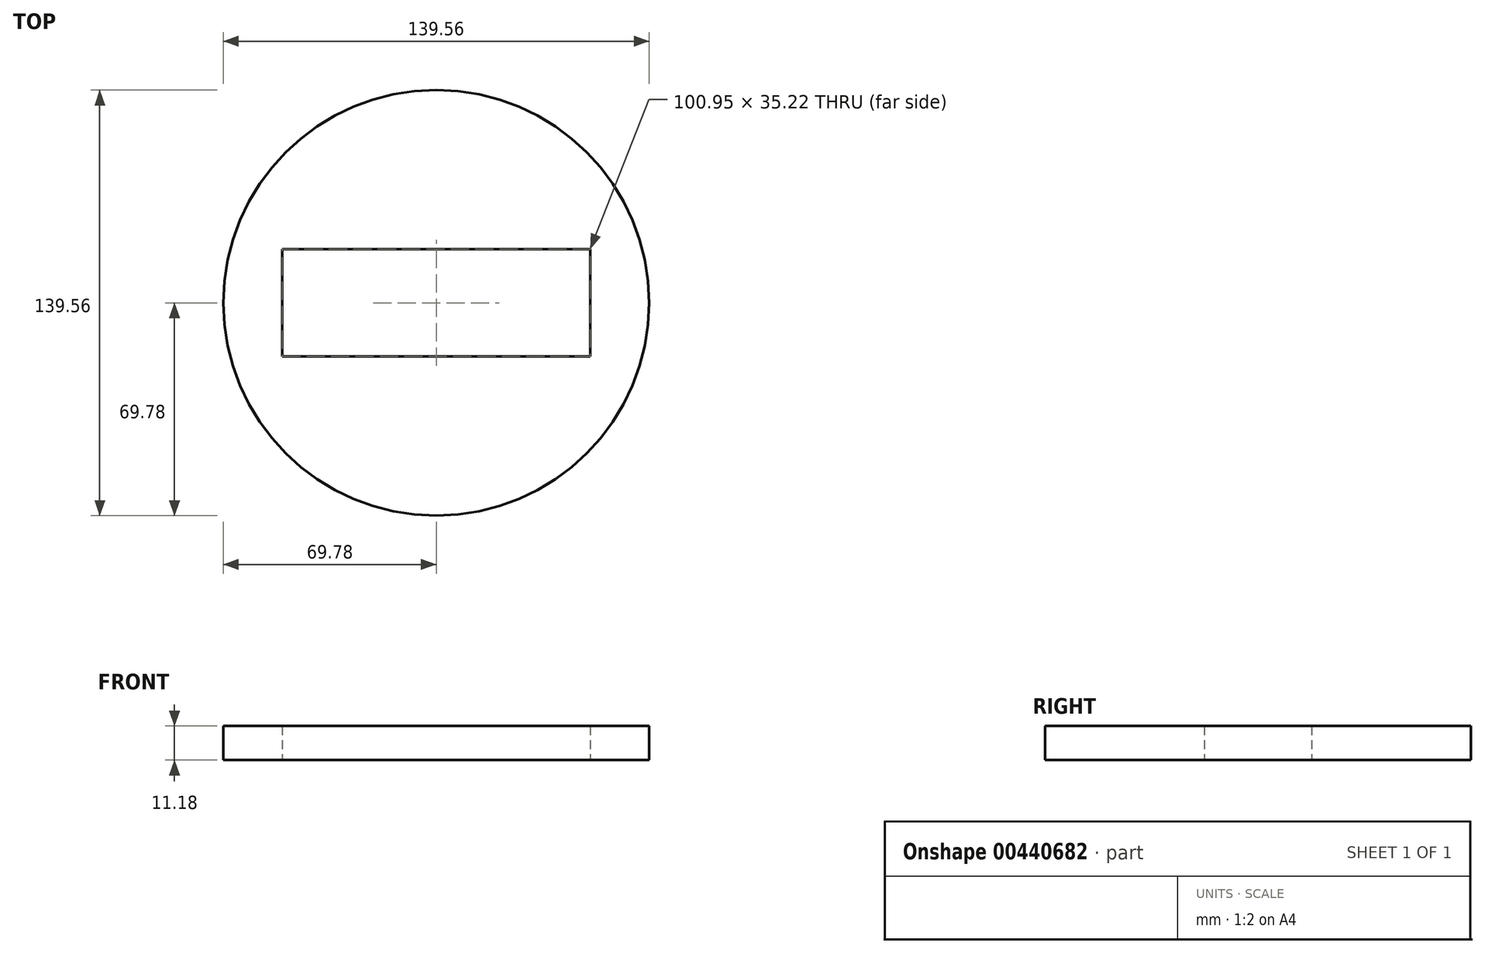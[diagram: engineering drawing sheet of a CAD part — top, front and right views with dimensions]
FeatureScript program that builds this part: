
annotation { "Feature Type Name" : "Feature", "Feature Type Description" : "" }
export const myFeature = defineFeature(function(context is Context, id is Id, definition is map)
    precondition{}
    {
        {
            var Q0;
            Q0=qCreatedBy(makeId("Top.planeOp"),FACE);
            var sketch = newSketch(context, id + "F0", { "sketchPlane" : qUnion([Q0])});
            skCircle(sketch, "E0", {"center": v(0, 0) * mm, "radius": 69.78 * mm});
            skLineSegment(sketch, "E1.bottom", {"start": v(50.48, -17.6) * mm, "end": v(-50.48, -17.6) * mm});
            skLineSegment(sketch, "E1.top", {"start": v(50.48, 17.6) * mm, "end": v(-50.48, 17.6) * mm});
            skLineSegment(sketch, "E1.left", {"start": v(50.48, -17.6) * mm, "end": v(50.48, 17.6) * mm});
            skLineSegment(sketch, "E1.right", {"start": v(-50.48, -17.6) * mm, "end": v(-50.48, 17.6) * mm});
            skSolve(sketch);
        }
        {
            var Q0;
            Q0 = qSketchRegion(id + "F0", true);
            extrude(context, id + "F1", {"entities" : qUnion([Q0]), "depth" : 11.18 * mm});
        }
    });
